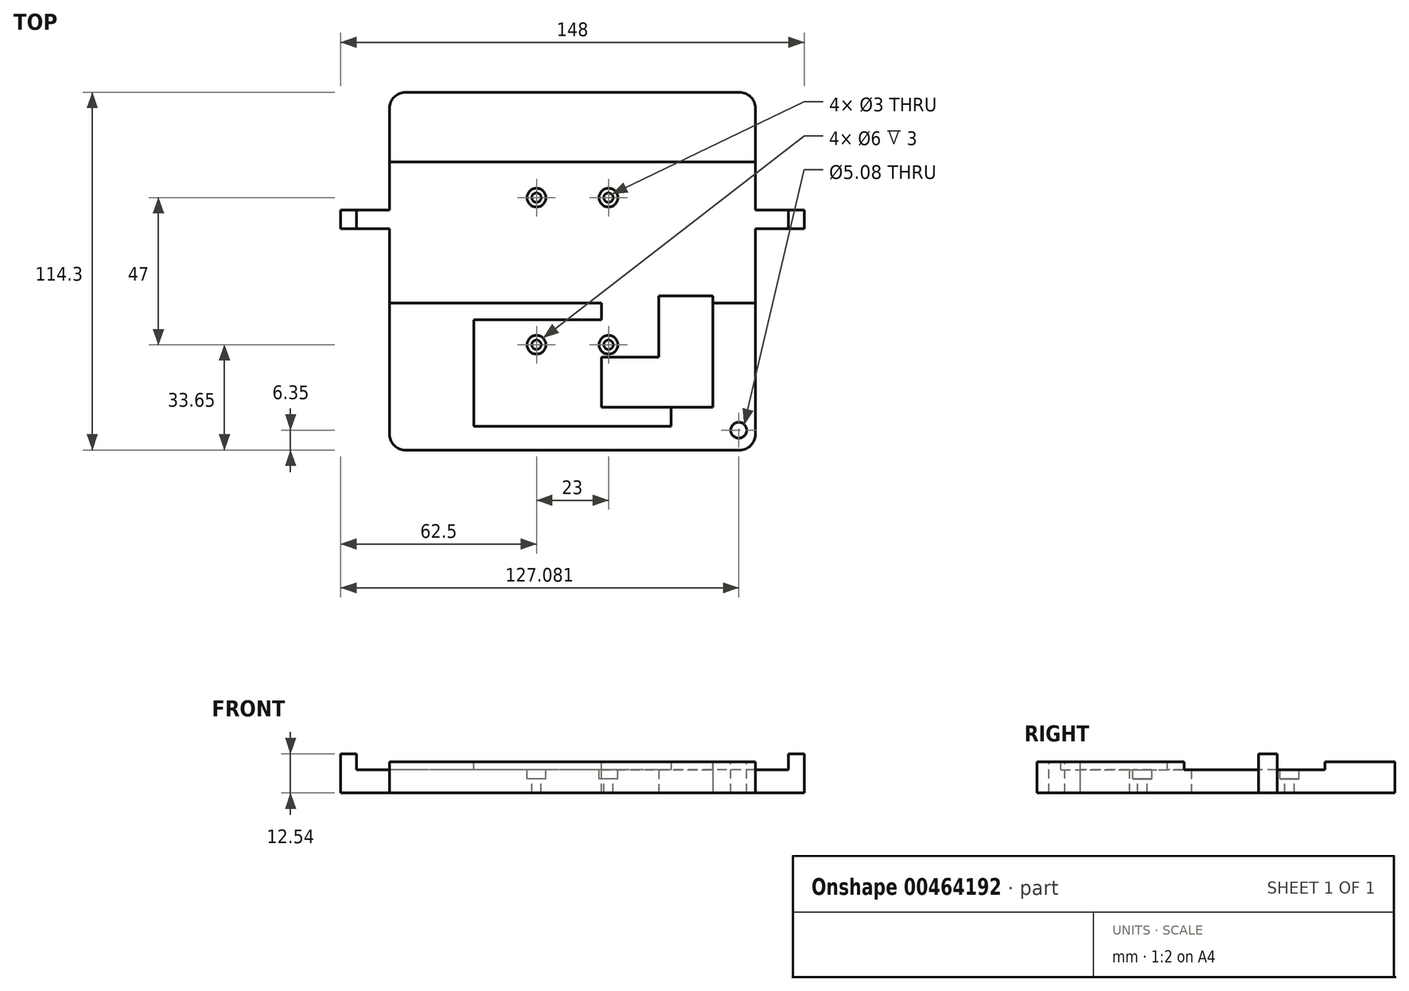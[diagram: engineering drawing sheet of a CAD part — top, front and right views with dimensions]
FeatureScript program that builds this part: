
annotation { "Feature Type Name" : "Feature", "Feature Type Description" : "" }
export const myFeature = defineFeature(function(context is Context, id is Id, definition is map)
    precondition{}
    {
        {
            var Q0;
            Q0=qCreatedBy(makeId("Top.planeOp"),FACE);
            var sketch = newSketch(context, id + "F0", { "sketchPlane" : qUnion([Q0])});
            skLineSegment(sketch, "E0.bottom", {"start": v(58.42, -57.15) * mm, "end": v(-58.42, -57.15) * mm});
            skLineSegment(sketch, "E0.top", {"start": v(58.42, 57.15) * mm, "end": v(-58.42, 57.15) * mm});
            skLineSegment(sketch, "E0.left", {"start": v(58.42, -57.15) * mm, "end": v(58.42, 57.15) * mm});
            skLineSegment(sketch, "E0.right", {"start": v(-58.42, -57.15) * mm, "end": v(-58.42, 57.15) * mm});
            skPoint(sketch, "E0.middle", {"position": v(0, 0) * mm});
            skSolve(sketch);
        }
        {
            var Q0;
            Q0=makeQuery(id+"F0.imprint","IMPRINT",FACE,{"disambiguationData":[TD([[makeQuery(id+"F0.imprint","IMPRINT",EDGE,{"derivedFrom":sQuery(id+"F0.wireOp",EDGE,"E0.bottom")}),-1.0]])]});
            extrude(context, id + "F1", {"entities" : qUnion([Q0]), "depth" : 10 * mm});
        }
        {
            var Q0;
            Q0=makeQuery(id+"F1.opExtrude","CAP_FACE",FACE,{"disambiguationData":[OSD([sQuery(id+"F0.wireOp",EDGE,"E0.bottom"),sQuery(id+"F0.wireOp",EDGE,"E0.top"),sQuery(id+"F0.wireOp",EDGE,"E0.left"),sQuery(id+"F0.wireOp",EDGE,"E0.right")])],"isStart":false});
            var sketch = newSketch(context, id + "F2", { "sketchPlane" : qUnion([Q0])});
            skCircle(sketch, "E1", {"center": v(53.08, -50.8) * mm, "radius": 4.5 * mm});
            skCircle(sketch, "E2", {"center": v(53.08, -50.8) * mm, "radius": 2.54 * mm});
            skLineSegment(sketch, "E3.bottom", {"start": v(58.08, -55.8) * mm, "end": v(48.08, -55.8) * mm});
            skLineSegment(sketch, "E3.top", {"start": v(58.08, -45.8) * mm, "end": v(48.08, -45.8) * mm});
            skLineSegment(sketch, "E3.left", {"start": v(58.08, -55.8) * mm, "end": v(58.08, -45.8) * mm});
            skLineSegment(sketch, "E3.right", {"start": v(48.08, -55.8) * mm, "end": v(48.08, -45.8) * mm});
            skSolve(sketch);
        }
        {
            var Q0;
            Q0=makeQuery(id+"F1.opExtrude","SWEPT_EDGE",EDGE,{"disambiguationData":[OSD([sQuery(id+"F0.wireOp",EDGE,"E0.bottom"),sQuery(id+"F0.wireOp",EDGE,"E0.left")])]});
            var Q1;
            Q1=makeQuery(id+"F1.opExtrude","SWEPT_EDGE",EDGE,{"disambiguationData":[OSD([sQuery(id+"F0.wireOp",EDGE,"E0.bottom"),sQuery(id+"F0.wireOp",EDGE,"E0.right")])]});
            var Q2;
            Q2=makeQuery(id+"F1.opExtrude","SWEPT_EDGE",EDGE,{"disambiguationData":[OSD([sQuery(id+"F0.wireOp",EDGE,"E0.top"),sQuery(id+"F0.wireOp",EDGE,"E0.left")])]});
            var Q3;
            Q3=makeQuery(id+"F1.opExtrude","SWEPT_EDGE",EDGE,{"disambiguationData":[OSD([sQuery(id+"F0.wireOp",EDGE,"E0.top"),sQuery(id+"F0.wireOp",EDGE,"E0.right")])]});
            fillet(context, id + "F3", {"entities" : qUnion([Q0, Q1, Q2, Q3]), "radius" : 5.08 * mm, "tangentPropagation" : true, "allowEdgeOverflow" : false});
        }
        {
            var Q0;
            Q0=makeQuery(id+"FvLwfkEbHAAyH91_1.boolean.opBoolean","SPLIT",FACE,{"disambiguationData":[TD([makeQuery(id+"FvLwfkEbHAAyH91_1.opExtrude","SWEPT_FACE",FACE,{"disambiguationData":[OSD([sQuery(id+"F2.wireOp",EDGE,"E2")])]})])],"derivedFrom":makeQuery(id+"F1.opExtrude","CAP_FACE",FACE,{"disambiguationData":[OSD([sQuery(id+"F0.wireOp",EDGE,"E0.bottom"),sQuery(id+"F0.wireOp",EDGE,"E0.top"),sQuery(id+"F0.wireOp",EDGE,"E0.left"),sQuery(id+"F0.wireOp",EDGE,"E0.right")])],"isStart":false})});
            var sketch = newSketch(context, id + "F4", { "sketchPlane" : qUnion([Q0])});
            skCircle(sketch, "E4", {"center": v(53.08, -50.8) * mm, "radius": 2.54 * mm});
            skSolve(sketch);
        }
        {
            var Q0;
            Q0=qSketchRegion(id+"F4",true);
            extrude(context, id + "F5", {"entities" : qUnion([Q0]), "operationType" : NewBodyOperationType.REMOVE, "oppositeDirection" : true, "depth" : 21.59 * mm, "offsetDistance" : 25 * mm});
        }
        {
            var Q0;
            Q0=qCreatedBy(makeId("Top.planeOp"),FACE);
            var sketch = newSketch(context, id + "F6", { "sketchPlane" : qUnion([Q0])});
            skLineSegment(sketch, "E5.bottom", {"start": v(9.27, -7.9) * mm, "end": v(44.83, -7.9) * mm});
            skLineSegment(sketch, "E5.top", {"start": v(9.27, -43.46) * mm, "end": v(44.83, -43.46) * mm});
            skLineSegment(sketch, "E5.left", {"start": v(9.27, -7.9) * mm, "end": v(9.27, -43.46) * mm});
            skLineSegment(sketch, "E5.right", {"start": v(44.83, -7.9) * mm, "end": v(44.83, -43.46) * mm});
            skSolve(sketch);
        }
        {
            var Q0;
            Q0=qSketchRegion(id+"F6",true);
            extrude(context, id + "F7", {"entities" : qUnion([Q0]), "operationType" : NewBodyOperationType.REMOVE, "depth" : 53.1 * mm});
        }
        {
            var Q0;
            Q0=makeQuery(id+"F2.imprint","IMPRINT",FACE,{"disambiguationData":[TD([[makeQuery(id+"F2.imprint","IMPRINT",EDGE,{"derivedFrom":sQuery(id+"F2.wireOp",EDGE,"E1")}),-1.0]])]});
            var sketch = newSketch(context, id + "F8", { "sketchPlane" : qUnion([Q0])});
            skPoint(sketch, "E6.middle", {"position": v(0, 0) * mm});
            skLineSegment(sketch, "E7.bottom", {"start": v(69, -10.15) * mm, "end": v(-69, -10.15) * mm});
            skLineSegment(sketch, "E7.top", {"start": v(69, 34.85) * mm, "end": v(-69, 34.85) * mm});
            skLineSegment(sketch, "E7.left", {"start": v(69, -10.15) * mm, "end": v(69, 34.85) * mm});
            skLineSegment(sketch, "E7.right", {"start": v(-69, -10.15) * mm, "end": v(-69, 34.85) * mm});
            skPoint(sketch, "E7.middle", {"position": v(0, 12.35) * mm});
            skPoint(sketch, "E7.cornerSnap0", {"position": v(69, -10.15) * mm});
            skLineSegment(sketch, "E8.bottom", {"start": v(31.5, -49.5) * mm, "end": v(-31.5, -49.5) * mm});
            skLineSegment(sketch, "E8.top", {"start": v(31.5, -15.5) * mm, "end": v(-31.5, -15.5) * mm});
            skLineSegment(sketch, "E8.left", {"start": v(31.5, -49.5) * mm, "end": v(31.5, -15.5) * mm});
            skLineSegment(sketch, "E8.right", {"start": v(-31.5, -49.5) * mm, "end": v(-31.5, -15.5) * mm});
            skPoint(sketch, "E8.middle", {"position": v(0, -32.5) * mm});
            skSolve(sketch);
        }
        {
            var Q0;
            Q0=qSketchRegion(id+"F8",true);
            extrude(context, id + "F9", {"entities" : qUnion([Q0]), "operationType" : NewBodyOperationType.REMOVE, "oppositeDirection" : true, "depth" : 2.54 * mm, "offsetDistance" : 25 * mm});
        }
        {
            var Q0;
            Q0=makeQuery(id+"F9.boolean.opBoolean","COPY",FACE,{"derivedFrom":makeQuery(id+"F9.opExtrude","CAP_FACE",FACE,{"disambiguationData":[OSD([sQuery(id+"F8.wireOp",EDGE,"E7.bottom"),sQuery(id+"F8.wireOp",EDGE,"E7.top"),sQuery(id+"F8.wireOp",EDGE,"E7.left"),sQuery(id+"F8.wireOp",EDGE,"E7.right")])],"isStart":false})});
            var sketch = newSketch(context, id + "F10", { "sketchPlane" : qUnion([Q0])});
            skLineSegment(sketch, "E9.bottom", {"start": v(74, 19.5) * mm, "end": v(-74, 19.5) * mm});
            skLineSegment(sketch, "E9.top", {"start": v(74, 13.54) * mm, "end": v(-74, 13.54) * mm});
            skLineSegment(sketch, "E9.left", {"start": v(74, 19.5) * mm, "end": v(74, 13.54) * mm});
            skLineSegment(sketch, "E9.right", {"start": v(-74, 19.5) * mm, "end": v(-74, 13.54) * mm});
            skPoint(sketch, "E9.middle", {"position": v(0, 16.53) * mm});
            skSolve(sketch);
        }
        {
            var Q0;
            Q0 = qSketchRegion(id + "F10", true);
            extrude(context, id + "F11", {"entities" : qUnion([Q0]), "operationType" : NewBodyOperationType.ADD, "oppositeDirection" : true, "depth" : 7.46 * mm, "offsetDistance" : 25 * mm});
        }
        {
            var Q0;
            Q0=makeQuery(id+"F11.boolean.opBoolean","MERGE",FACE,{"derivedFrom":[makeQuery(id+"F9.boolean.opBoolean","COPY",FACE,{"derivedFrom":makeQuery(id+"F9.opExtrude","CAP_FACE",FACE,{"disambiguationData":[OSD([sQuery(id+"F8.wireOp",EDGE,"E7.bottom"),sQuery(id+"F8.wireOp",EDGE,"E7.top"),sQuery(id+"F8.wireOp",EDGE,"E7.left"),sQuery(id+"F8.wireOp",EDGE,"E7.right")])],"isStart":false})}),makeQuery(id+"F11.opExtrude","CAP_FACE",FACE,{"disambiguationData":[OSD([sQuery(id+"F10.wireOp",EDGE,"E9.bottom"),sQuery(id+"F10.wireOp",EDGE,"E9.top"),sQuery(id+"F10.wireOp",EDGE,"E9.left"),sQuery(id+"F10.wireOp",EDGE,"E9.right")])],"isStart":true})]});
            var sketch = newSketch(context, id + "F12", { "sketchPlane" : qUnion([Q0])});
            skLineSegment(sketch, "E10.bottom", {"start": v(-74, 19.5) * mm, "end": v(-69, 19.5) * mm});
            skLineSegment(sketch, "E10.top", {"start": v(-74, 13.54) * mm, "end": v(-69, 13.54) * mm});
            skLineSegment(sketch, "E10.left", {"start": v(-74, 19.5) * mm, "end": v(-74, 13.54) * mm});
            skLineSegment(sketch, "E10.right", {"start": v(-69, 19.5) * mm, "end": v(-69, 13.54) * mm});
            skLineSegment(sketch, "E11.bottom", {"start": v(74, 19.5) * mm, "end": v(69, 19.5) * mm});
            skLineSegment(sketch, "E11.top", {"start": v(74, 13.54) * mm, "end": v(69, 13.54) * mm});
            skLineSegment(sketch, "E11.left", {"start": v(74, 19.5) * mm, "end": v(74, 13.54) * mm});
            skLineSegment(sketch, "E11.right", {"start": v(69, 19.5) * mm, "end": v(69, 13.54) * mm});
            skSolve(sketch);
        }
        {
            var Q0;
            Q0=makeQuery(id+"F12.imprint","IMPRINT",FACE,{"disambiguationData":[TD([[makeQuery(id+"F12.imprint","IMPRINT",EDGE,{"derivedFrom":sQuery(id+"F12.wireOp",EDGE,"E11.bottom")}),1.0]])]});
            var Q1;
            Q1=makeQuery(id+"F12.imprint","IMPRINT",FACE,{"disambiguationData":[TD([[makeQuery(id+"F12.imprint","IMPRINT",EDGE,{"derivedFrom":sQuery(id+"F12.wireOp",EDGE,"E10.bottom")}),1.0]])]});
            extrude(context, id + "F13", {"entities" : qUnion([Q0, Q1]), "operationType" : NewBodyOperationType.ADD, "depth" : 5.08 * mm, "offsetDistance" : 25 * mm});
        }
        {
            var Q0;
            Q0=makeQuery(id+"F11.boolean.opBoolean","MERGE",FACE,{"derivedFrom":[makeQuery(id+"F9.boolean.opBoolean","COPY",FACE,{"derivedFrom":makeQuery(id+"F9.opExtrude","CAP_FACE",FACE,{"disambiguationData":[OSD([sQuery(id+"F8.wireOp",EDGE,"E7.bottom"),sQuery(id+"F8.wireOp",EDGE,"E7.top"),sQuery(id+"F8.wireOp",EDGE,"E7.left"),sQuery(id+"F8.wireOp",EDGE,"E7.right")])],"isStart":false})}),makeQuery(id+"F11.opExtrude","CAP_FACE",FACE,{"disambiguationData":[OSD([sQuery(id+"F10.wireOp",EDGE,"E9.bottom"),sQuery(id+"F10.wireOp",EDGE,"E9.top"),sQuery(id+"F10.wireOp",EDGE,"E9.left"),sQuery(id+"F10.wireOp",EDGE,"E9.right")])],"isStart":true})]});
            var sketch = newSketch(context, id + "F14", { "sketchPlane" : qUnion([Q0])});
            skLineSegment(sketch, "E12.bottom", {"start": v(27.5, -27.5) * mm, "end": v(-27.5, -27.5) * mm});
            skLineSegment(sketch, "E12.top", {"start": v(27.5, 27.5) * mm, "end": v(-27.5, 27.5) * mm});
            skLineSegment(sketch, "E12.left", {"start": v(27.5, -27.5) * mm, "end": v(27.5, 27.5) * mm});
            skLineSegment(sketch, "E12.right", {"start": v(-27.5, -27.5) * mm, "end": v(-27.5, 27.5) * mm});
            skPoint(sketch, "E12.middle", {"position": v(0, 0) * mm});
            skSolve(sketch);
        }
        {
            var Q0;
            Q0 = qSketchRegion(id + "F14", true);
            extrude(context, id + "F15", {"entities" : qUnion([Q0]), "operationType" : NewBodyOperationType.ADD, "oppositeDirection" : true, "depth" : 7.46 * mm, "offsetDistance" : 25 * mm});
        }
        {
            var Q0;
            Q0=makeQuery(id+"F15.boolean.opBoolean","MERGE",FACE,{"derivedFrom":[makeQuery(id+"F9.boolean.opBoolean","COPY",FACE,{"derivedFrom":makeQuery(id+"F9.opExtrude","CAP_FACE",FACE,{"disambiguationData":[OSD([sQuery(id+"F8.wireOp",EDGE,"E8.bottom"),sQuery(id+"F8.wireOp",EDGE,"E8.top"),sQuery(id+"F8.wireOp",EDGE,"E8.left"),sQuery(id+"F8.wireOp",EDGE,"E8.right")])],"isStart":false})}),makeQuery(id+"F11.boolean.opBoolean","MERGE",FACE,{"derivedFrom":[makeQuery(id+"F9.boolean.opBoolean","COPY",FACE,{"derivedFrom":makeQuery(id+"F9.opExtrude","CAP_FACE",FACE,{"disambiguationData":[OSD([sQuery(id+"F8.wireOp",EDGE,"E7.bottom"),sQuery(id+"F8.wireOp",EDGE,"E7.top"),sQuery(id+"F8.wireOp",EDGE,"E7.left"),sQuery(id+"F8.wireOp",EDGE,"E7.right")])],"isStart":false})}),makeQuery(id+"F11.opExtrude","CAP_FACE",FACE,{"disambiguationData":[OSD([sQuery(id+"F10.wireOp",EDGE,"E9.bottom"),sQuery(id+"F10.wireOp",EDGE,"E9.top"),sQuery(id+"F10.wireOp",EDGE,"E9.left"),sQuery(id+"F10.wireOp",EDGE,"E9.right")])],"isStart":true})]}),makeQuery(id+"F15.opExtrude","CAP_FACE",FACE,{"disambiguationData":[OSD([sQuery(id+"F14.wireOp",EDGE,"E12.bottom"),sQuery(id+"F14.wireOp",EDGE,"E12.top"),sQuery(id+"F14.wireOp",EDGE,"E12.left"),sQuery(id+"F14.wireOp",EDGE,"E12.right")])],"isStart":true})]});
            var sketch = newSketch(context, id + "F16", { "sketchPlane" : qUnion([Q0])});
            skPoint(sketch, "E13.middle", {"position": v(0, 0) * mm});
            skCircle(sketch, "E14", {"center": v(11.5, 23.5) * mm, "radius": 1.5 * mm});
            skCircle(sketch, "E15", {"center": v(-11.5, -23.5) * mm, "radius": 1.5 * mm});
            skCircle(sketch, "E16", {"center": v(11.5, -23.5) * mm, "radius": 1.5 * mm});
            skCircle(sketch, "E17", {"center": v(-11.5, 23.5) * mm, "radius": 1.5 * mm});
            skSolve(sketch);
        }
        {
            var Q0;
            Q0 = qSketchRegion(id + "F16", true);
            extrude(context, id + "F17", {"entities" : qUnion([Q0]), "operationType" : NewBodyOperationType.REMOVE, "oppositeDirection" : true, "depth" : 25 * mm, "offsetDistance" : 25 * mm});
        }
        {
            var Q0;
            Q0=makeQuery(id+"F15.boolean.opBoolean","MERGE",FACE,{"derivedFrom":[makeQuery(id+"F9.boolean.opBoolean","COPY",FACE,{"derivedFrom":makeQuery(id+"F9.opExtrude","CAP_FACE",FACE,{"disambiguationData":[OSD([sQuery(id+"F8.wireOp",EDGE,"E8.bottom"),sQuery(id+"F8.wireOp",EDGE,"E8.top"),sQuery(id+"F8.wireOp",EDGE,"E8.left"),sQuery(id+"F8.wireOp",EDGE,"E8.right")])],"isStart":false})}),makeQuery(id+"F11.boolean.opBoolean","MERGE",FACE,{"derivedFrom":[makeQuery(id+"F9.boolean.opBoolean","COPY",FACE,{"derivedFrom":makeQuery(id+"F9.opExtrude","CAP_FACE",FACE,{"disambiguationData":[OSD([sQuery(id+"F8.wireOp",EDGE,"E7.bottom"),sQuery(id+"F8.wireOp",EDGE,"E7.top"),sQuery(id+"F8.wireOp",EDGE,"E7.left"),sQuery(id+"F8.wireOp",EDGE,"E7.right")])],"isStart":false})}),makeQuery(id+"F11.opExtrude","CAP_FACE",FACE,{"disambiguationData":[OSD([sQuery(id+"F10.wireOp",EDGE,"E9.bottom"),sQuery(id+"F10.wireOp",EDGE,"E9.top"),sQuery(id+"F10.wireOp",EDGE,"E9.left"),sQuery(id+"F10.wireOp",EDGE,"E9.right")])],"isStart":true})]}),makeQuery(id+"F15.opExtrude","CAP_FACE",FACE,{"disambiguationData":[OSD([sQuery(id+"F14.wireOp",EDGE,"E12.bottom"),sQuery(id+"F14.wireOp",EDGE,"E12.top"),sQuery(id+"F14.wireOp",EDGE,"E12.left"),sQuery(id+"F14.wireOp",EDGE,"E12.right")])],"isStart":true})]});
            var sketch = newSketch(context, id + "F18", { "sketchPlane" : qUnion([Q0])});
            skCircle(sketch, "E18", {"center": v(11.5, 23.5) * mm, "radius": 3 * mm});
            skCircle(sketch, "E19", {"center": v(-11.5, 23.5) * mm, "radius": 3 * mm});
            skCircle(sketch, "E20", {"center": v(-11.5, -23.5) * mm, "radius": 3 * mm});
            skCircle(sketch, "E21", {"center": v(11.5, -23.5) * mm, "radius": 3 * mm});
            skSolve(sketch);
        }
        {
            var Q0;
            Q0 = qSketchRegion(id + "F18", true);
            extrude(context, id + "F19", {"entities" : qUnion([Q0]), "operationType" : NewBodyOperationType.REMOVE, "oppositeDirection" : true, "depth" : 3 * mm, "offsetDistance" : 25 * mm});
        }
    });
